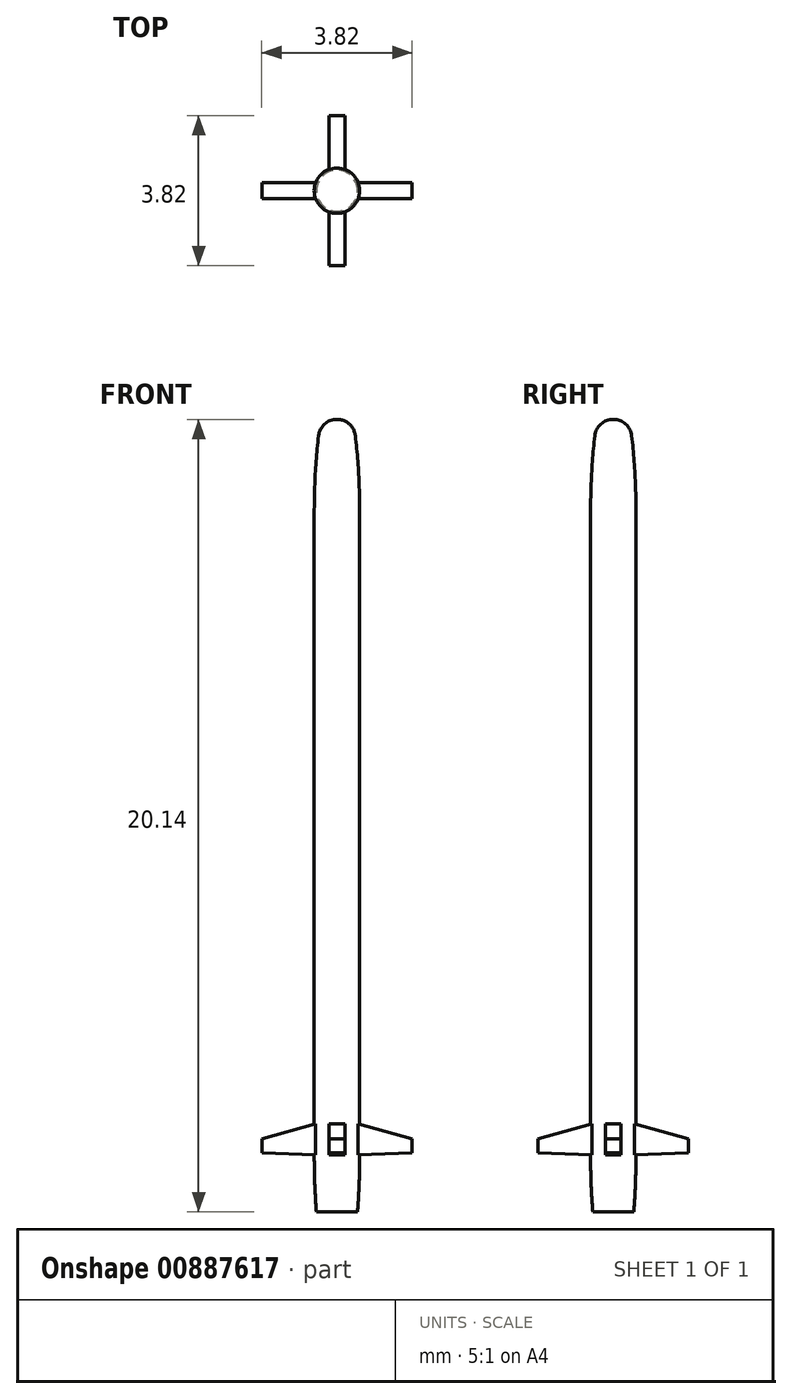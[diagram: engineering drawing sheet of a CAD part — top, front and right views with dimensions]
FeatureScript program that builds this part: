
annotation { "Feature Type Name" : "Feature", "Feature Type Description" : "" }
export const myFeature = defineFeature(function(context is Context, id is Id, definition is map)
    precondition{}
    {
        {
            var Q0;
            Q0=qCreatedBy(makeId("Front.planeOp"),FACE);
            var sketch = newSketch(context, id + "F0", { "sketchPlane" : qUnion([Q0])});
            skLineSegment(sketch, "E0", {"start": v(0, 0) * mm, "end": v(0, 20.14) * mm});
            skLineSegment(sketch, "E1", {"start": v(0.58, 17.85) * mm, "end": v(0.58, 0) * mm});
            skLineSegment(sketch, "E2", {"start": v(0.58, 0) * mm, "end": v(0, 0) * mm});
            skArc(sketch, "E3", {"start": v(0.52, 0) * mm, "mid": v(0.56, 0.7) * mm, "end": v(0.58, 1.39) * mm});
            skArc(sketch, "E4", {"start": v(0.47, 19.72) * mm, "mid": v(0.31, 20.02) * mm, "end": v(0, 20.14) * mm});
            skArc(sketch, "E5", {"start": v(0.58, 17.85) * mm, "mid": v(0.55, 18.79) * mm, "end": v(0.47, 19.72) * mm});
            skSolve(sketch);
        }
        {
            var Q0;
            {var subQ0=sQuery(id+"F0.wireOp",EDGE,"mrwio9nY-PsAZ-Zbfy-NhIU-sYq0QVbgGXAG");Q0=makeQuery(id+"F0.imprint","IMPRINT",FACE,{"disambiguationData":[TD([[makeQuery(id+"F0.imprint","IMPRINT",EDGE,{"derivedFrom":subQ0}),-1.0]])]});}
            var Q1;
            {var subQ7=sQuery(id+"F0.wireOp",EDGE,"E0");Q1=makeQuery(id+"F0.imprint","IMPRINT",FACE,{"disambiguationData":[TD([[makeQuery(id+"F0.imprint","IMPRINT",EDGE,{"derivedFrom":subQ7}),-1.0]])]});}
            var Q2;
            Q2=sQuery(id+"F0.wireOp",EDGE,"E0");
            revolve(context, id + "F1", {"surfaceOperationType" : NewSurfaceOperationType.NEW, "entities" : qUnion([Q0, Q1]), "axis" : qUnion([Q2]), "revolveType" : RevolveType.FULL});
        }
        {
            var Q0;
            Q0=qCreatedBy(makeId("Front.planeOp"),FACE);
            var sketch = newSketch(context, id + "F2", { "sketchPlane" : qUnion([Q0])});
            skLineSegment(sketch, "E6", {"start": v(0, 0) * mm, "end": v(0, 11.11) * mm});
            skLineSegment(sketch, "E7", {"start": v(0.4, 11.39) * mm, "end": v(0.4, 2.29) * mm});
            skLineSegment(sketch, "E8", {"start": v(0.4, 2.29) * mm, "end": v(1.9, 1.85) * mm});
            skLineSegment(sketch, "E9", {"start": v(0.58, 0) * mm, "end": v(0.58, 32.87) * mm, "construction": true});
            skPoint(sketch, "E10", {"position": v(0.58, 2.24) * mm});
            skLineSegment(sketch, "E11", {"start": v(0, 1.44) * mm, "end": v(1.9, 1.5) * mm});
            skLineSegment(sketch, "E12", {"start": v(1.9, 1.5) * mm, "end": v(1.9, 1.85) * mm});
            skLineSegment(sketch, "E13.0", {"start": v(0.58, 1.39) * mm, "end": v(-0.58, 1.39) * mm});
            skPoint(sketch, "E14", {"position": v(0.58, 1.46) * mm});
            skLineSegment(sketch, "E15", {"start": v(0, 11.11) * mm, "end": v(0.4, 11.39) * mm});
            skSolve(sketch);
        }
        {
            var Q0;
            Q0=qSketchRegion(id+"F2",true);
            extrude(context, id + "F3", {"entities" : qUnion([Q0]), "operationType" : NewBodyOperationType.ADD, "depth" : .4 * mm, "offsetDistance" : 25 * mm, "symmetric" : true});
        }
        {
            var Q0;
            Q0=makeQuery(id+"F1.opRevolve","SWEPT_BODY",BODY,{"disambiguationData":[OSD([sQuery(id+"F0.wireOp",EDGE,"E0"),sQuery(id+"F0.wireOp",EDGE,"E1"),sQuery(id+"F0.wireOp",EDGE,"E2"),sQuery(id+"F0.wireOp",EDGE,"2EiOItwe-9FNA-eY8p-DkXH-AMy5AHyUmzZA"),sQuery(id+"F0.wireOp",EDGE,"lF35QjYl-MEgV-fRWE-0Yr6-Bt5vS8A7brRf")])]});
            var Q1;
            Q1=makeQuery(id+"F1.opRevolve","SWEPT_FACE",FACE,{"disambiguationData":[OSD([sQuery(id+"F0.wireOp",EDGE,"E1")])]});
            circularPattern(context, id + "F4", {"operationType" : NewBodyOperationType.ADD, "entities" : qUnion([Q0]), "axis" : qUnion([Q1]), "angle" : 360 * degree, "instanceCount" : 4, "equalSpace" : true, "computeTransformsWithoutBuiltin" : true});
        }
    });
